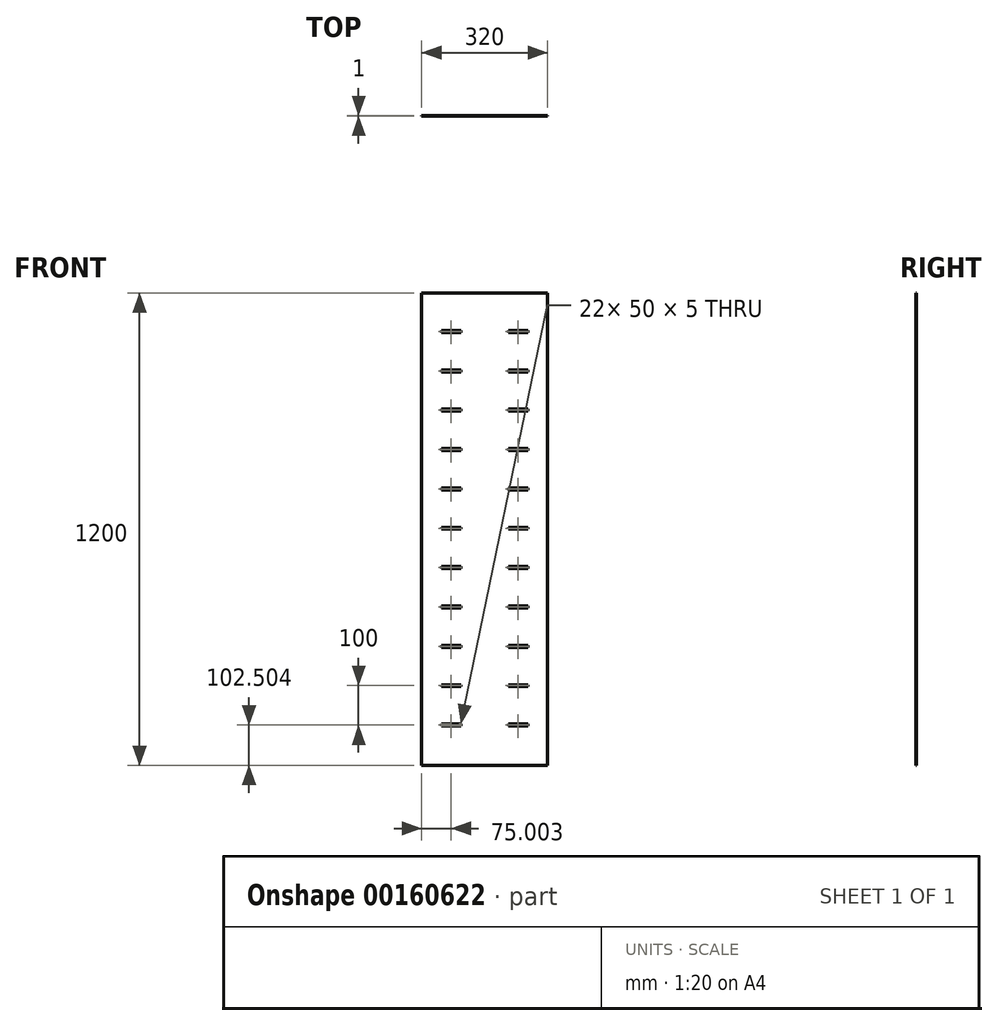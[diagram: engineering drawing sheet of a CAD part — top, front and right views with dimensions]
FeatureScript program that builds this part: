
annotation { "Feature Type Name" : "Feature", "Feature Type Description" : "" }
export const myFeature = defineFeature(function(context is Context, id is Id, definition is map)
    precondition{}
    {
        {
            var Q0;
            Q0=qCreatedBy(makeId("Front.planeOp"),FACE);
            var sketch = newSketch(context, id + "F0", { "sketchPlane" : qUnion([Q0])});
            skLineSegment(sketch, "E0.bottom", {"start": v(-312.16, 1182.44) * mm, "end": v(7.84, 1182.44) * mm});
            skLineSegment(sketch, "E0.top", {"start": v(-312.16, -17.56) * mm, "end": v(7.84, -17.56) * mm});
            skLineSegment(sketch, "E0.left", {"start": v(-312.16, 1182.44) * mm, "end": v(-312.16, -17.56) * mm});
            skLineSegment(sketch, "E0.right", {"start": v(7.84, 1182.44) * mm, "end": v(7.84, -17.56) * mm});
            skLineSegment(sketch, "E1.bottom", {"start": v(-262.16, 82.44) * mm, "end": v(-212.16, 82.44) * mm});
            skLineSegment(sketch, "E1.top", {"start": v(-262.16, 87.44) * mm, "end": v(-212.16, 87.44) * mm});
            skLineSegment(sketch, "E1.left", {"start": v(-262.16, 82.44) * mm, "end": v(-262.16, 87.44) * mm});
            skLineSegment(sketch, "E1.right", {"start": v(-212.16, 82.44) * mm, "end": v(-212.16, 87.44) * mm});
            skLineSegment(sketch, "E2.bottom", {"start": v(-92.16, 82.44) * mm, "end": v(-42.16, 82.44) * mm});
            skLineSegment(sketch, "E2.top", {"start": v(-92.16, 87.44) * mm, "end": v(-42.16, 87.44) * mm});
            skLineSegment(sketch, "E2.left", {"start": v(-92.16, 82.44) * mm, "end": v(-92.16, 87.44) * mm});
            skLineSegment(sketch, "E2.right", {"start": v(-42.16, 82.44) * mm, "end": v(-42.16, 87.44) * mm});
            skLineSegment(sketch, "E3.0.1.0", {"start": v(-262.16, 187.44) * mm, "end": v(-212.16, 187.44) * mm});
            skLineSegment(sketch, "E3.0.1.1", {"start": v(-262.16, 182.44) * mm, "end": v(-212.16, 182.44) * mm});
            skLineSegment(sketch, "E3.0.1.2", {"start": v(-92.16, 182.44) * mm, "end": v(-42.16, 182.44) * mm});
            skLineSegment(sketch, "E3.0.1.3", {"start": v(-92.16, 187.44) * mm, "end": v(-42.16, 187.44) * mm});
            skLineSegment(sketch, "E3.0.1.4", {"start": v(-212.16, 182.44) * mm, "end": v(-212.16, 187.44) * mm});
            skLineSegment(sketch, "E3.0.1.5", {"start": v(-262.16, 182.44) * mm, "end": v(-262.16, 187.44) * mm});
            skLineSegment(sketch, "E3.0.1.6", {"start": v(-92.16, 182.44) * mm, "end": v(-92.16, 187.44) * mm});
            skLineSegment(sketch, "E3.0.1.7", {"start": v(-42.16, 182.44) * mm, "end": v(-42.16, 187.44) * mm});
            skLineSegment(sketch, "E3.0.2.0", {"start": v(-262.16, 287.44) * mm, "end": v(-212.16, 287.44) * mm});
            skLineSegment(sketch, "E3.0.2.1", {"start": v(-262.16, 282.44) * mm, "end": v(-212.16, 282.44) * mm});
            skLineSegment(sketch, "E3.0.2.2", {"start": v(-92.16, 282.44) * mm, "end": v(-42.16, 282.44) * mm});
            skLineSegment(sketch, "E3.0.2.3", {"start": v(-92.16, 287.44) * mm, "end": v(-42.16, 287.44) * mm});
            skLineSegment(sketch, "E3.0.2.4", {"start": v(-212.16, 282.44) * mm, "end": v(-212.16, 287.44) * mm});
            skLineSegment(sketch, "E3.0.2.5", {"start": v(-262.16, 282.44) * mm, "end": v(-262.16, 287.44) * mm});
            skLineSegment(sketch, "E3.0.2.6", {"start": v(-92.16, 282.44) * mm, "end": v(-92.16, 287.44) * mm});
            skLineSegment(sketch, "E3.0.2.7", {"start": v(-42.16, 282.44) * mm, "end": v(-42.16, 287.44) * mm});
            skLineSegment(sketch, "E3.0.3.0", {"start": v(-262.16, 387.44) * mm, "end": v(-212.16, 387.44) * mm});
            skLineSegment(sketch, "E3.0.3.1", {"start": v(-262.16, 382.44) * mm, "end": v(-212.16, 382.44) * mm});
            skLineSegment(sketch, "E3.0.3.2", {"start": v(-92.16, 382.44) * mm, "end": v(-42.16, 382.44) * mm});
            skLineSegment(sketch, "E3.0.3.3", {"start": v(-92.16, 387.44) * mm, "end": v(-42.16, 387.44) * mm});
            skLineSegment(sketch, "E3.0.3.4", {"start": v(-212.16, 382.44) * mm, "end": v(-212.16, 387.44) * mm});
            skLineSegment(sketch, "E3.0.3.5", {"start": v(-262.16, 382.44) * mm, "end": v(-262.16, 387.44) * mm});
            skLineSegment(sketch, "E3.0.3.6", {"start": v(-92.16, 382.44) * mm, "end": v(-92.16, 387.44) * mm});
            skLineSegment(sketch, "E3.0.3.7", {"start": v(-42.16, 382.44) * mm, "end": v(-42.16, 387.44) * mm});
            skLineSegment(sketch, "E3.0.4.0", {"start": v(-262.16, 487.44) * mm, "end": v(-212.16, 487.44) * mm});
            skLineSegment(sketch, "E3.0.4.1", {"start": v(-262.16, 482.44) * mm, "end": v(-212.16, 482.44) * mm});
            skLineSegment(sketch, "E3.0.4.2", {"start": v(-92.16, 482.44) * mm, "end": v(-42.16, 482.44) * mm});
            skLineSegment(sketch, "E3.0.4.3", {"start": v(-92.16, 487.44) * mm, "end": v(-42.16, 487.44) * mm});
            skLineSegment(sketch, "E3.0.4.4", {"start": v(-212.16, 482.44) * mm, "end": v(-212.16, 487.44) * mm});
            skLineSegment(sketch, "E3.0.4.5", {"start": v(-262.16, 482.44) * mm, "end": v(-262.16, 487.44) * mm});
            skLineSegment(sketch, "E3.0.4.6", {"start": v(-92.16, 482.44) * mm, "end": v(-92.16, 487.44) * mm});
            skLineSegment(sketch, "E3.0.4.7", {"start": v(-42.16, 482.44) * mm, "end": v(-42.16, 487.44) * mm});
            skLineSegment(sketch, "E3.0.5.0", {"start": v(-262.16, 587.44) * mm, "end": v(-212.16, 587.44) * mm});
            skLineSegment(sketch, "E3.0.5.1", {"start": v(-262.16, 582.44) * mm, "end": v(-212.16, 582.44) * mm});
            skLineSegment(sketch, "E3.0.5.2", {"start": v(-92.16, 582.44) * mm, "end": v(-42.16, 582.44) * mm});
            skLineSegment(sketch, "E3.0.5.3", {"start": v(-92.16, 587.44) * mm, "end": v(-42.16, 587.44) * mm});
            skLineSegment(sketch, "E3.0.5.4", {"start": v(-212.16, 582.44) * mm, "end": v(-212.16, 587.44) * mm});
            skLineSegment(sketch, "E3.0.5.5", {"start": v(-262.16, 582.44) * mm, "end": v(-262.16, 587.44) * mm});
            skLineSegment(sketch, "E3.0.5.6", {"start": v(-92.16, 582.44) * mm, "end": v(-92.16, 587.44) * mm});
            skLineSegment(sketch, "E3.0.5.7", {"start": v(-42.16, 582.44) * mm, "end": v(-42.16, 587.44) * mm});
            skLineSegment(sketch, "E3.0.6.0", {"start": v(-262.16, 687.44) * mm, "end": v(-212.16, 687.44) * mm});
            skLineSegment(sketch, "E3.0.6.1", {"start": v(-262.16, 682.44) * mm, "end": v(-212.16, 682.44) * mm});
            skLineSegment(sketch, "E3.0.6.2", {"start": v(-92.16, 682.44) * mm, "end": v(-42.16, 682.44) * mm});
            skLineSegment(sketch, "E3.0.6.3", {"start": v(-92.16, 687.44) * mm, "end": v(-42.16, 687.44) * mm});
            skLineSegment(sketch, "E3.0.6.4", {"start": v(-212.16, 682.44) * mm, "end": v(-212.16, 687.44) * mm});
            skLineSegment(sketch, "E3.0.6.5", {"start": v(-262.16, 682.44) * mm, "end": v(-262.16, 687.44) * mm});
            skLineSegment(sketch, "E3.0.6.6", {"start": v(-92.16, 682.44) * mm, "end": v(-92.16, 687.44) * mm});
            skLineSegment(sketch, "E3.0.6.7", {"start": v(-42.16, 682.44) * mm, "end": v(-42.16, 687.44) * mm});
            skLineSegment(sketch, "E3.0.7.0", {"start": v(-262.16, 787.44) * mm, "end": v(-212.16, 787.44) * mm});
            skLineSegment(sketch, "E3.0.7.1", {"start": v(-262.16, 782.44) * mm, "end": v(-212.16, 782.44) * mm});
            skLineSegment(sketch, "E3.0.7.2", {"start": v(-92.16, 782.44) * mm, "end": v(-42.16, 782.44) * mm});
            skLineSegment(sketch, "E3.0.7.3", {"start": v(-92.16, 787.44) * mm, "end": v(-42.16, 787.44) * mm});
            skLineSegment(sketch, "E3.0.7.4", {"start": v(-212.16, 782.44) * mm, "end": v(-212.16, 787.44) * mm});
            skLineSegment(sketch, "E3.0.7.5", {"start": v(-262.16, 782.44) * mm, "end": v(-262.16, 787.44) * mm});
            skLineSegment(sketch, "E3.0.7.6", {"start": v(-92.16, 782.44) * mm, "end": v(-92.16, 787.44) * mm});
            skLineSegment(sketch, "E3.0.7.7", {"start": v(-42.16, 782.44) * mm, "end": v(-42.16, 787.44) * mm});
            skLineSegment(sketch, "E3.0.8.0", {"start": v(-262.16, 887.44) * mm, "end": v(-212.16, 887.44) * mm});
            skLineSegment(sketch, "E3.0.8.1", {"start": v(-262.16, 882.44) * mm, "end": v(-212.16, 882.44) * mm});
            skLineSegment(sketch, "E3.0.8.2", {"start": v(-92.16, 882.44) * mm, "end": v(-42.16, 882.44) * mm});
            skLineSegment(sketch, "E3.0.8.3", {"start": v(-92.16, 887.44) * mm, "end": v(-42.16, 887.44) * mm});
            skLineSegment(sketch, "E3.0.8.4", {"start": v(-212.16, 882.44) * mm, "end": v(-212.16, 887.44) * mm});
            skLineSegment(sketch, "E3.0.8.5", {"start": v(-262.16, 882.44) * mm, "end": v(-262.16, 887.44) * mm});
            skLineSegment(sketch, "E3.0.8.6", {"start": v(-92.16, 882.44) * mm, "end": v(-92.16, 887.44) * mm});
            skLineSegment(sketch, "E3.0.8.7", {"start": v(-42.16, 882.44) * mm, "end": v(-42.16, 887.44) * mm});
            skLineSegment(sketch, "E3.0.9.0", {"start": v(-262.16, 987.44) * mm, "end": v(-212.16, 987.44) * mm});
            skLineSegment(sketch, "E3.0.9.1", {"start": v(-262.16, 982.44) * mm, "end": v(-212.16, 982.44) * mm});
            skLineSegment(sketch, "E3.0.9.2", {"start": v(-92.16, 982.44) * mm, "end": v(-42.16, 982.44) * mm});
            skLineSegment(sketch, "E3.0.9.3", {"start": v(-92.16, 987.44) * mm, "end": v(-42.16, 987.44) * mm});
            skLineSegment(sketch, "E3.0.9.4", {"start": v(-212.16, 982.44) * mm, "end": v(-212.16, 987.44) * mm});
            skLineSegment(sketch, "E3.0.9.5", {"start": v(-262.16, 982.44) * mm, "end": v(-262.16, 987.44) * mm});
            skLineSegment(sketch, "E3.0.9.6", {"start": v(-92.16, 982.44) * mm, "end": v(-92.16, 987.44) * mm});
            skLineSegment(sketch, "E3.0.9.7", {"start": v(-42.16, 982.44) * mm, "end": v(-42.16, 987.44) * mm});
            skLineSegment(sketch, "E3.0.10.0", {"start": v(-262.16, 1087.44) * mm, "end": v(-212.16, 1087.44) * mm});
            skLineSegment(sketch, "E3.0.10.1", {"start": v(-262.16, 1082.44) * mm, "end": v(-212.16, 1082.44) * mm});
            skLineSegment(sketch, "E3.0.10.2", {"start": v(-92.16, 1082.44) * mm, "end": v(-42.16, 1082.44) * mm});
            skLineSegment(sketch, "E3.0.10.3", {"start": v(-92.16, 1087.44) * mm, "end": v(-42.16, 1087.44) * mm});
            skLineSegment(sketch, "E3.0.10.4", {"start": v(-212.16, 1082.44) * mm, "end": v(-212.16, 1087.44) * mm});
            skLineSegment(sketch, "E3.0.10.5", {"start": v(-262.16, 1082.44) * mm, "end": v(-262.16, 1087.44) * mm});
            skLineSegment(sketch, "E3.0.10.6", {"start": v(-92.16, 1082.44) * mm, "end": v(-92.16, 1087.44) * mm});
            skLineSegment(sketch, "E3.0.10.7", {"start": v(-42.16, 1082.44) * mm, "end": v(-42.16, 1087.44) * mm});
            skLineSegment(sketch, "E3.direction1", {"start": v(-262.16, 82.44) * mm, "end": v(-237.16, 82.44) * mm, "construction": true});
            skLineSegment(sketch, "E3.direction2", {"start": v(-262.16, 82.44) * mm, "end": v(-262.16, 182.44) * mm, "construction": true});
            skSolve(sketch);
        }
        {
            var Q0;
            Q0 = qSketchRegion(id + "F0", true);
            extrude(context, id + "F1", {"entities" : qUnion([Q0]), "depth" : 1 * mm});
        }
    });
